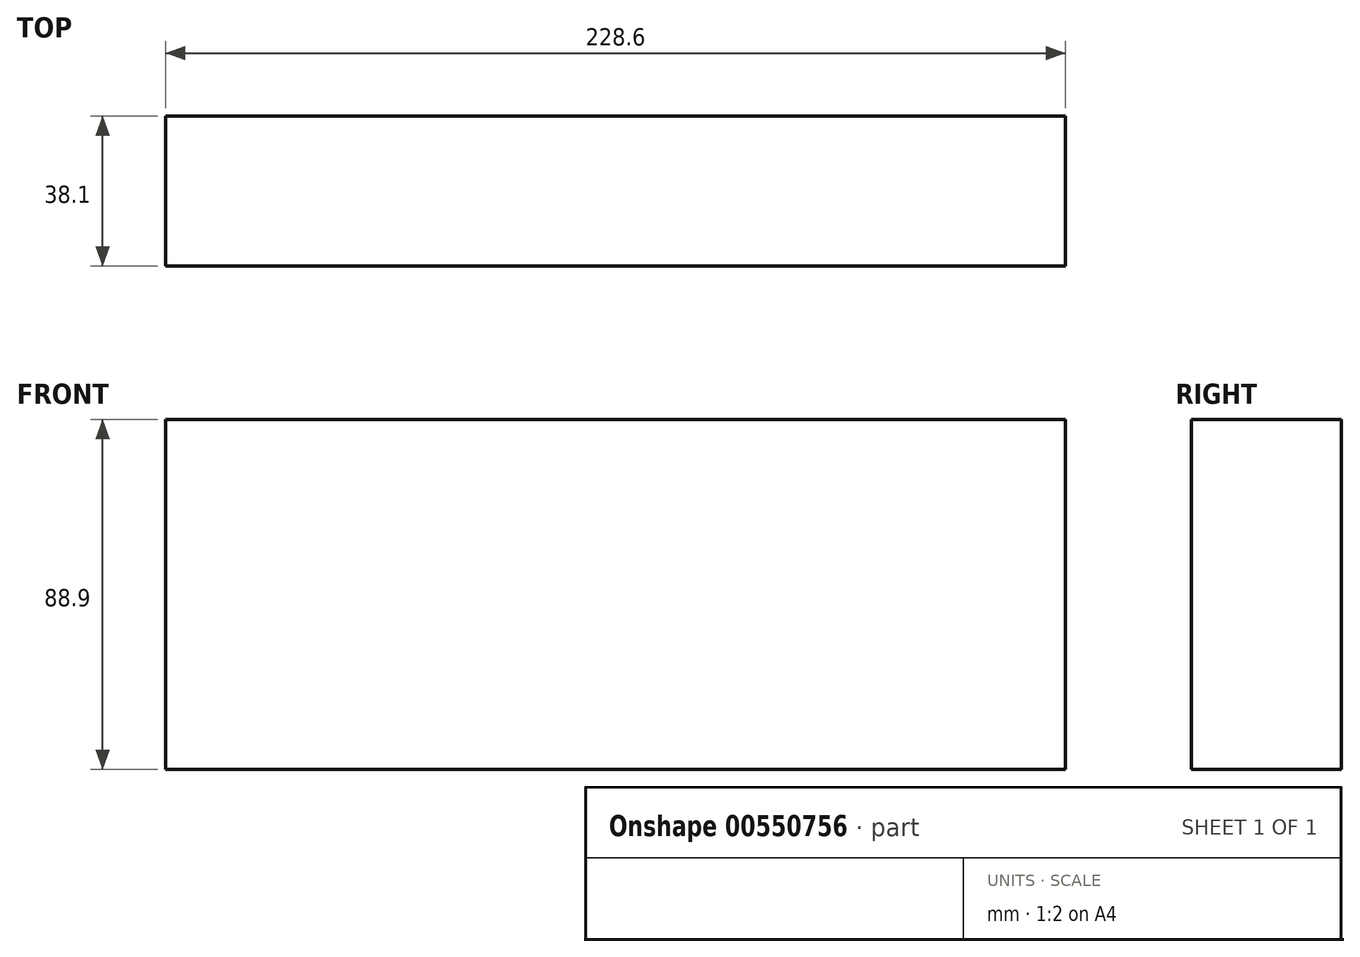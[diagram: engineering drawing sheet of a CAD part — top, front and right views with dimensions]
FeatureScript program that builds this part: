
annotation { "Feature Type Name" : "Feature", "Feature Type Description" : "" }
export const myFeature = defineFeature(function(context is Context, id is Id, definition is map)
    precondition{}
    {
        {
            var Q0;
            Q0=qCreatedBy(makeId("Right.planeOp"),FACE);
            var sketch = newSketch(context, id + "F0", { "sketchPlane" : qUnion([Q0])});
            skLineSegment(sketch, "E0.bottom", {"start": v(0, 0) * mm, "end": v(38.1, 0) * mm});
            skLineSegment(sketch, "E0.top", {"start": v(0, 88.9) * mm, "end": v(38.1, 88.9) * mm});
            skLineSegment(sketch, "E0.left", {"start": v(0, 0) * mm, "end": v(0, 88.9) * mm});
            skLineSegment(sketch, "E0.right", {"start": v(38.1, 0) * mm, "end": v(38.1, 88.9) * mm});
            skSolve(sketch);
        }
        {
            var Q0;
            Q0 = qSketchRegion(id + "F0", true);
            extrude(context, id + "F1", {"entities" : qUnion([Q0]), "oppositeDirection" : true, "depth" : 228.6 * mm, "offsetDistance" : 25.4 * mm});
        }
    });
